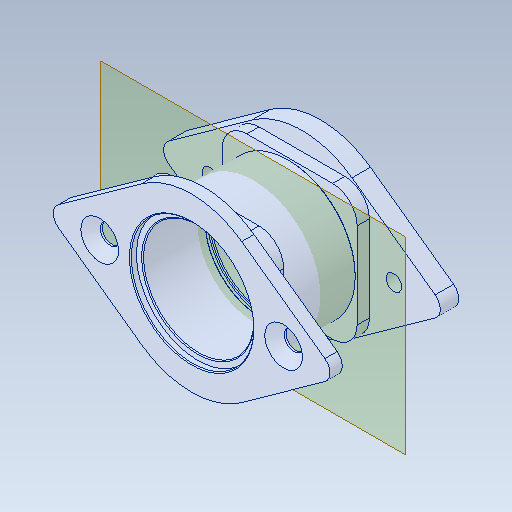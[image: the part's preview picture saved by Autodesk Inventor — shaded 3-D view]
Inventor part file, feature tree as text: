
AUTODESK INVENTOR PART (.ipt)
format: ipt  version: 2020 (Build 240168000, 168)  size: 228,864 bytes
history: native  units: in
note: dims shown in document units (in); Inventor stores cm internally (conversion verified against a paired STEP export)
features: other x2, plane x1
ambient origin geometry x8: Origin, YZ Plane, XZ Plane, XY Plane, X Axis, Y Axis, Z Axis, Center Point
bodies: Solid1 (feature_tree), Solid2 (feature_tree)
feature tree (3):
  plane  "Work Plane1"
  other  "217-3436-001 Rev2_1:1"
  other  "217-3436-002 Rev2_2:1"
